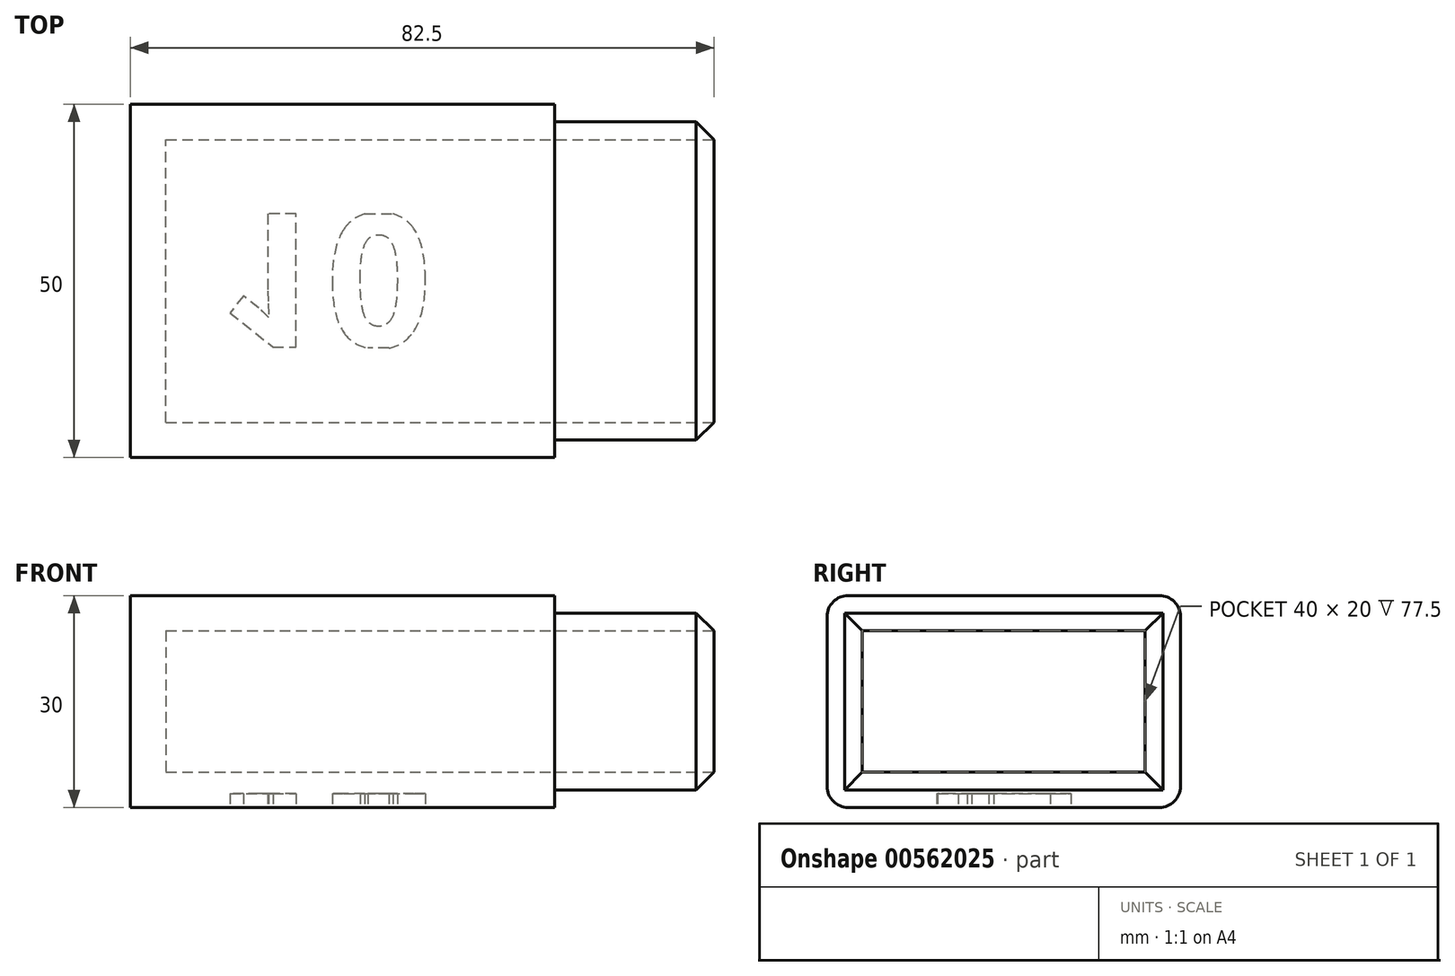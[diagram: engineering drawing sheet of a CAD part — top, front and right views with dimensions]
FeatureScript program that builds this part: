
annotation { "Feature Type Name" : "Feature", "Feature Type Description" : "" }
export const myFeature = defineFeature(function(context is Context, id is Id, definition is map)
    precondition{}
    {
        {
            var Q0;
            Q0=qCreatedBy(makeId("Right.planeOp"),FACE);
            var sketch = newSketch(context, id + "F0", { "sketchPlane" : qUnion([Q0])});
            skLineSegment(sketch, "E0.bottom", {"start": v(-9.65, 13.7) * mm, "end": v(30.35, 13.7) * mm});
            skLineSegment(sketch, "E0.top", {"start": v(-9.65, -6.3) * mm, "end": v(30.35, -6.3) * mm});
            skLineSegment(sketch, "E0.left", {"start": v(-9.65, 13.7) * mm, "end": v(-9.65, -6.3) * mm});
            skLineSegment(sketch, "E0.right", {"start": v(30.35, 13.7) * mm, "end": v(30.35, -6.3) * mm});
            skLineSegment(sketch, "E1.0", {"start": v(-14.65, 18.7) * mm, "end": v(35.35, 18.7) * mm});
            skLineSegment(sketch, "E1.1", {"start": v(-14.65, 18.7) * mm, "end": v(-14.65, -11.3) * mm});
            skLineSegment(sketch, "E1.2", {"start": v(-14.65, -11.3) * mm, "end": v(35.35, -11.3) * mm});
            skLineSegment(sketch, "E1.3", {"start": v(35.35, 18.7) * mm, "end": v(35.35, -11.3) * mm});
            skLineSegment(sketch, "E2.0", {"start": v(-12.15, 16.2) * mm, "end": v(-12.15, -8.8) * mm});
            skLineSegment(sketch, "E2.1", {"start": v(-12.15, 16.2) * mm, "end": v(32.85, 16.2) * mm});
            skLineSegment(sketch, "E2.2", {"start": v(32.85, 16.2) * mm, "end": v(32.85, -8.8) * mm});
            skLineSegment(sketch, "E2.3", {"start": v(-12.15, -8.8) * mm, "end": v(32.85, -8.8) * mm});
            skSolve(sketch);
        }
        {
            var Q0;
            Q0=makeQuery(id+"F0.imprint","IMPRINT",FACE,{"disambiguationData":[TD([[makeQuery(id+"F0.imprint","IMPRINT",EDGE,{"derivedFrom":sQuery(id+"F0.wireOp",EDGE,"E0.bottom")}),1.0]])]});
            var Q1;
            Q1=makeQuery(id+"F0.imprint","IMPRINT",FACE,{"disambiguationData":[TD([[makeQuery(id+"F0.imprint","IMPRINT",EDGE,{"derivedFrom":sQuery(id+"F0.wireOp",EDGE,"E0.bottom")}),-1.0]])]});
            var Q2;
            Q2=makeQuery(id+"F0.imprint","IMPRINT",FACE,{"disambiguationData":[TD([[makeQuery(id+"F0.imprint","IMPRINT",EDGE,{"derivedFrom":sQuery(id+"F0.wireOp",EDGE,"E1.0")}),-1.0]])]});
            extrude(context, id + "F1", {"entities" : qUnion([Q0, Q1, Q2]), "oppositeDirection" : true, "depth" : 60 * mm, "offsetDistance" : 25 * mm});
        }
        {
            var Q0;
            Q0=makeQuery(id+"F0.imprint","IMPRINT",FACE,{"disambiguationData":[TD([[makeQuery(id+"F0.imprint","IMPRINT",EDGE,{"derivedFrom":sQuery(id+"F0.wireOp",EDGE,"E0.bottom")}),-1.0]])]});
            extrude(context, id + "F2", {"entities" : qUnion([Q0]), "operationType" : NewBodyOperationType.REMOVE, "oppositeDirection" : true, "depth" : 55 * mm, "offsetDistance" : 25 * mm});
        }
        {
            var Q0;
            Q0=makeQuery(id+"F0.imprint","IMPRINT",FACE,{"disambiguationData":[TD([[makeQuery(id+"F0.imprint","IMPRINT",EDGE,{"derivedFrom":sQuery(id+"F0.wireOp",EDGE,"E0.bottom")}),1.0]])]});
            extrude(context, id + "F3", {"entities" : qUnion([Q0]), "operationType" : NewBodyOperationType.ADD, "depth" : 25 * mm, "offsetDistance" : 25 * mm});
        }
        {
            var Q0;
            Q0=makeQuery(id+"F3.opExtrude","CAP_EDGE",EDGE,{"disambiguationData":[OSD([sQuery(id+"F0.wireOp",EDGE,"E2.0")])],"isStart":false});
            var Q1;
            Q1=makeQuery(id+"F3.opExtrude","CAP_EDGE",EDGE,{"disambiguationData":[OSD([sQuery(id+"F0.wireOp",EDGE,"E2.3")])],"isStart":false});
            var Q2;
            Q2=makeQuery(id+"F3.opExtrude","CAP_EDGE",EDGE,{"disambiguationData":[OSD([sQuery(id+"F0.wireOp",EDGE,"E2.2")])],"isStart":false});
            var Q3;
            Q3=makeQuery(id+"F3.opExtrude","CAP_EDGE",EDGE,{"disambiguationData":[OSD([sQuery(id+"F0.wireOp",EDGE,"E2.1")])],"isStart":false});
            chamfer(context, id + "F4", {"entities" : qUnion([Q0, Q1, Q2, Q3]), "width" : 5 * mm, "tangentPropagation" : true});
        }
        {
            var Q0;
            Q0=makeQuery(id+"F1.opExtrude","SWEPT_EDGE",EDGE,{"disambiguationData":[OSD([sQuery(id+"F0.wireOp",EDGE,"E1.2"),sQuery(id+"F0.wireOp",EDGE,"E1.3")])]});
            var Q1;
            Q1=makeQuery(id+"F1.opExtrude","SWEPT_EDGE",EDGE,{"disambiguationData":[OSD([sQuery(id+"F0.wireOp",EDGE,"E1.0"),sQuery(id+"F0.wireOp",EDGE,"E1.3")])]});
            var Q2;
            Q2=makeQuery(id+"F1.opExtrude","SWEPT_EDGE",EDGE,{"disambiguationData":[OSD([sQuery(id+"F0.wireOp",EDGE,"E1.1"),sQuery(id+"F0.wireOp",EDGE,"E1.2")])]});
            var Q3;
            Q3=makeQuery(id+"F1.opExtrude","SWEPT_EDGE",EDGE,{"disambiguationData":[OSD([sQuery(id+"F0.wireOp",EDGE,"E1.0"),sQuery(id+"F0.wireOp",EDGE,"E1.1")])]});
            fillet(context, id + "F5", {"entities" : qUnion([Q0, Q1, Q2, Q3]), "radius" : 3 * mm, "tangentPropagation" : true, "allowEdgeOverflow" : false});
        }
        {
            var Q0;
            Q0=makeQuery(id+"F1.opExtrude","SWEPT_FACE",FACE,{"disambiguationData":[OSD([sQuery(id+"F0.wireOp",EDGE,"E1.2")])]});
            var sketch = newSketch(context, id + "F6", { "sketchPlane" : qUnion([Q0])});
            skLineSegment(sketch, "E3.0", {"start": v(-12.5, -19.85) * mm, "end": v(-12.5, -0.85) * mm});
            skLineSegment(sketch, "E3.1", {"start": v(-47.5, -19.85) * mm, "end": v(-12.5, -19.85) * mm});
            skLineSegment(sketch, "E3.2", {"start": v(-47.5, -0.85) * mm, "end": v(-47.5, -19.85) * mm});
            skLineSegment(sketch, "E3.3", {"start": v(-12.5, -0.85) * mm, "end": v(-47.5, -0.85) * mm});
            skText(sketch, "E4", { "text": "10", "fontName": "OpenSans-Bold.ttf"});
            const initialGuessF6  = {"E4": [-0.0475, -0.01985, 1, 0, 0.019]};
            skSetInitialGuess(sketch, initialGuessF6);
            skSolve(sketch);
        }
        {
            var Q0;
            Q0=makeQuery(id+"F6.imprint","IMPRINT",FACE,{"disambiguationData":[TD([[makeQuery(id+"F6.imprint","IMPRINT",EDGE,{"derivedFrom":sQuery(id+"F6.wireOp",EDGE,"E4.sketch_text.stroke-0")}),-1.0]])]});
            var Q1;
            {var subQ13=sQuery(id+"F6.wireOp",EDGE,"E4.sketch_text.stroke-10");Q1=makeQuery(id+"F6.imprint","IMPRINT",FACE,{"disambiguationData":[TD([[makeQuery(id+"F6.imprint","IMPRINT",EDGE,{"derivedFrom":subQ13}),-1.0]])]});}
            extrude(context, id + "F7", {"entities" : qUnion([Q0, Q1]), "operationType" : NewBodyOperationType.REMOVE, "oppositeDirection" : true, "depth" : 2 * mm, "offsetDistance" : 25 * mm});
        }
    });
